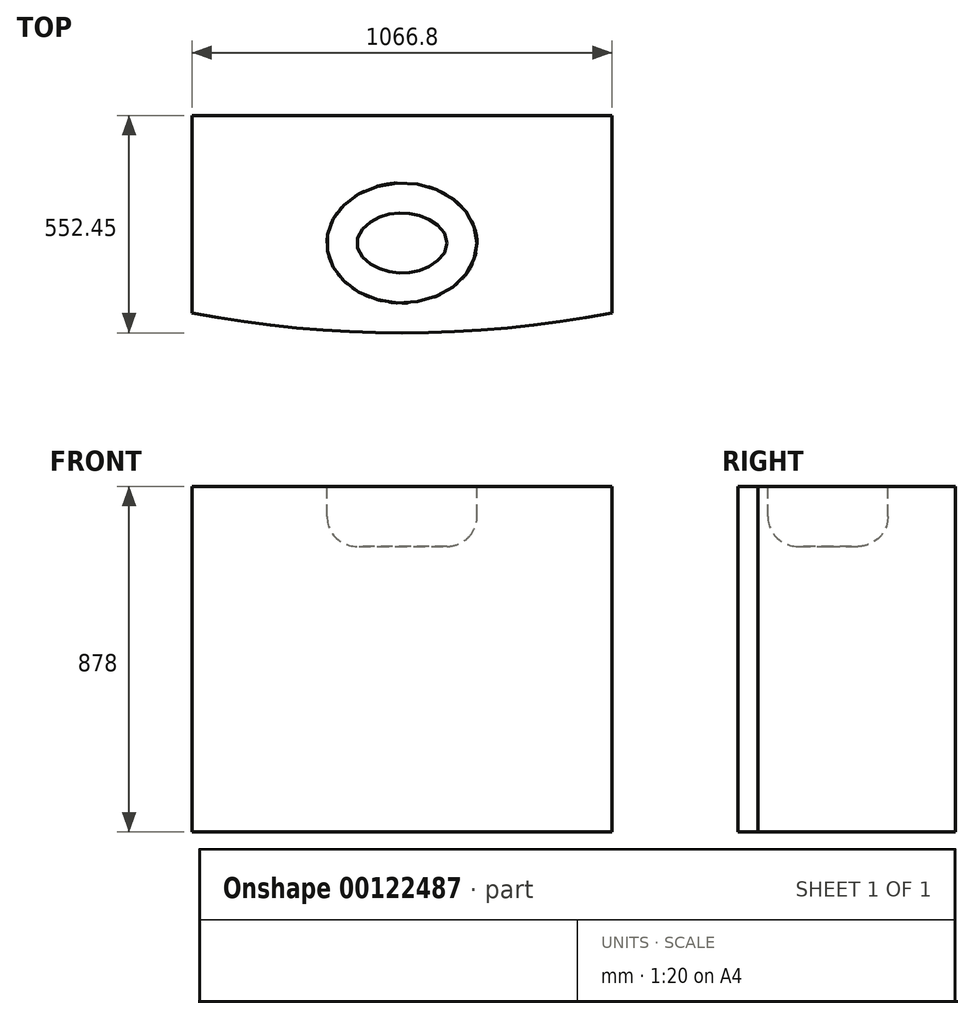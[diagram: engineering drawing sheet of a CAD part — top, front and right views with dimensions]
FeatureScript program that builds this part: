
annotation { "Feature Type Name" : "Feature", "Feature Type Description" : "" }
export const myFeature = defineFeature(function(context is Context, id is Id, definition is map)
    precondition{}
    {
        {
            var Q0;
            Q0=qCreatedBy(makeId("Top.planeOp"),FACE);
            var sketch = newSketch(context, id + "F0", { "sketchPlane" : qUnion([Q0])});
            skLineSegment(sketch, "E0.bottom", {"start": v(0, 0) * mm, "end": v(1066.8, 0) * mm});
            skLineSegment(sketch, "E0.left", {"start": v(0, 0) * mm, "end": v(0, -501.65) * mm});
            skLineSegment(sketch, "E0.right", {"start": v(1066.8, 0) * mm, "end": v(1066.8, -501.65) * mm});
            skArc(sketch, "E1", {"start": v(0, -501.65) * mm, "mid": v(533.4, -552.45) * mm, "end": v(1066.8, -501.65) * mm});
            skLineSegment(sketch, "E2", {"start": v(533.4, -552.45) * mm, "end": v(533.4, 0) * mm, "construction": true});
            skSolve(sketch);
        }
        {
            var Q0;
            Q0 = qSketchRegion(id + "F0", true);
            extrude(context, id + "F1", {"entities" : qUnion([Q0]), "depth" : 878 * mm});
        }
        {
            var Q0;
            Q0=makeQuery(id+"F1.opExtrude","CAP_FACE",FACE,{"disambiguationData":[OSD([sQuery(id+"F0.wireOp",EDGE,"E0.bottom"),sQuery(id+"F0.wireOp",EDGE,"E0.left"),sQuery(id+"F0.wireOp",EDGE,"E0.right"),sQuery(id+"F0.wireOp",EDGE,"E1")])],"isStart":false});
            var sketch = newSketch(context, id + "F2", { "sketchPlane" : qUnion([Q0])});
            skEllipse(sketch, "E3", {"center": v(533.4, -323.85) * mm, "majorRadius": 190.5 * mm, "minorRadius": 152.4 * mm, "majorAxis": v(1, 0)});
            skLineSegment(sketch, "E4", {"start": v(533.4, -323.85) * mm, "end": v(533.4, 0) * mm, "construction": true});
            skLineSegment(sketch, "E5", {"start": v(533.4, -552.45) * mm, "end": v(533.4, -476.25) * mm, "construction": true});
            skSolve(sketch);
        }
        {
            var Q0;
            Q0 = qSketchRegion(id + "F2", true);
            extrude(context, id + "F3", {"entities" : qUnion([Q0]), "operationType" : NewBodyOperationType.REMOVE, "oppositeDirection" : true, "depth" : 152.4 * mm});
        }
        {
            var Q0;
            Q0=makeQuery(id+"F3.boolean.opBoolean","COPY",EDGE,{"derivedFrom":makeQuery(id+"F3.opExtrude","CAP_EDGE",EDGE,{"disambiguationData":[OSD([sQuery(id+"F2.wireOp",EDGE,"E3")])],"isStart":false})});
            fillet(context, id + "F4", {"entities" : qUnion([Q0]), "radius" : 76.2 * mm, "tangentPropagation" : true, "allowEdgeOverflow" : false});
        }
    });
